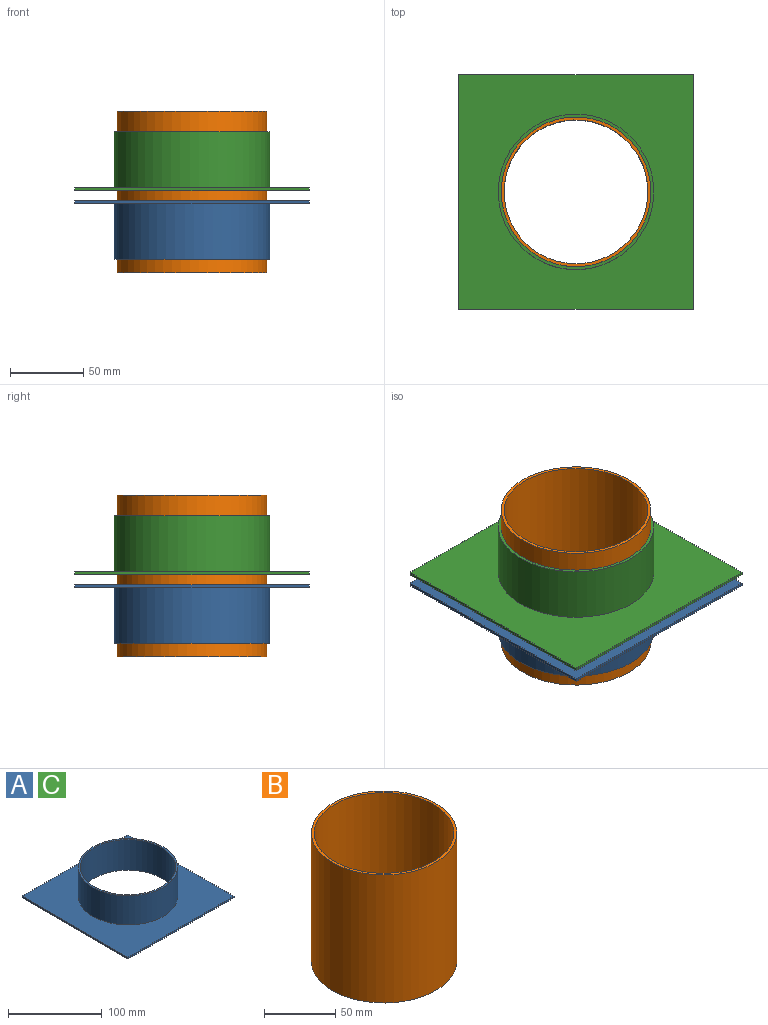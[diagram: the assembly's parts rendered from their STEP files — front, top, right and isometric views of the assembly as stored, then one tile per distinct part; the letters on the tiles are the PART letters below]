
ASSEMBLY  parts=3 mates=2
PART A: 9 faces, bbox 160x160x40 mm
  f0: plane 160x2mm, normal (1,0,0), area 320mm2, adj f1,f3,f4,f5
  f1: plane 160x2mm, normal (0,1,0), area 320mm2, adj f0,f2,f4,f5
  f2: plane 160x2mm, normal (-1,0,0), area 320mm2, adj f1,f3,f4,f5
  f3: plane 160x2mm, normal (0,-1,0), area 320mm2, adj f0,f2,f4,f5
  f4: plane 160x160mm, normal (0,0,1), area 16775.3mm2, adj f0,f1,f2,f3,f7
  f5: plane 160x160mm, normal (0,0,-1), area 17428.7mm2, adj f0,f1,f2,f3,f6
  f6: cylinder r=51mm len=102mm, axis (0,0,-1), area 12817.7mm2, adj f5,f8
  f7: cylinder r=53mm len=106mm, axis (0,0,-1), area 12654.3mm2, adj f4,f8
  f8: plane 106x106mm, normal (0,0,1), area 653.5mm2, adj f6,f7
PART B: 4 faces, bbox 102x102x110 mm
  f0: cylinder r=49mm len=110mm, axis (0,0,-1), area 33866.4mm2, adj f2,f3
  f1: cylinder r=51mm len=110mm, axis (0,0,-1), area 35248.7mm2, adj f2,f3
  f2: plane 102x102mm, normal (0,0,1), area 628.3mm2, adj f0,f1
  f3: plane 102x102mm, normal (0,0,-1), area 628.3mm2, adj f0,f1
PART C: same geometry as A
PLACE A rot(axis=(0,-1,0),180deg) t=(-78.65,-14.39,49.38)mm
PLACE B rot(axis=(0,1,0),0deg) t=(-78.65,-14.39,0.38)mm
PLACE C rot(axis=(0,1,0),0deg) t=(-78.65,-14.39,56.38)mm
MATE slider B.f0 <-> A.f6  axis (0,0,-1) through (-78.65,-14.39,0.38)mm
MATE slider C.f6 <-> A.f6  axis (0,0,-1) through (-78.65,-14.39,56.38)mm
